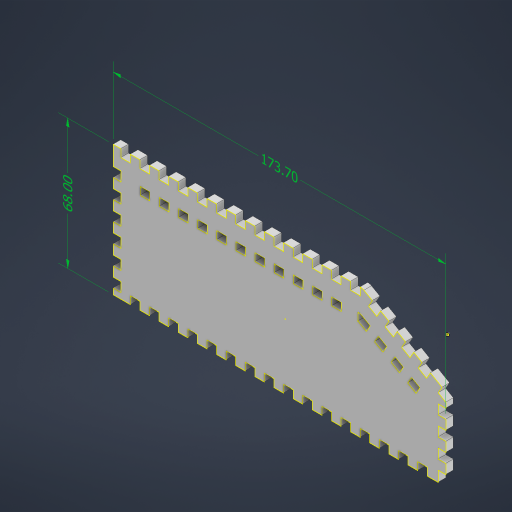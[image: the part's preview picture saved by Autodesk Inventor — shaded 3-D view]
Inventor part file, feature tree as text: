
AUTODESK INVENTOR PART (.ipt)
format: ipt  version: 2023 (Build 270158030, 158C)  size: 1,006,080 bytes
history: native  units: mm
features: extrude x5, sketch x5, other x3, direct_edit x3, move_body x3, delete_face x1, projected_geometry x1
ambient origin geometry x8: Origin, YZ Plane, XZ Plane, XY Plane, X Axis, Y Axis, Z Axis, Center Point
bodies: Solid1 (feature_tree)
feature tree (21):
  other  "Annotations"
  extrude  "Extrusion1"  Depth=60.0mm
  sketch  "Sketch2"  dims[d2=47.0mm d3=30.0deg]
  extrude  "Extrusion2"  TaperAngle=30.0deg  [1 undecoded]
  extrude  "Extrusion3"  Depth=4.0mm TaperAngle=0.0deg
  extrude  "Extrusion4"  Depth=4.0mm
  extrude  "Extrusion5"  Depth=5.0mm
  direct_edit  "Direct Edit1"
  delete_face  "Delete Face1"
  direct_edit  "Direct Edit2"
  direct_edit  "Direct Edit3"
  sketch  "Sketch7"  dims[d9=120.0mm d11=10.0mm d12=10.0mm d14=10.0mm d16=5.0mm d17=4.0mm d18=50.0mm d20=10.0mm d21=10.0mm d23=10.0mm d25=7.0mm d26=5.0mm d27=4.0mm d28=120.0mm d30=10.0mm d31=10.0mm d33=10.0mm d35=5.0mm d36=30.0deg d37=4.0mm d38=40.0mm d40=10.0mm d41=10.0mm d43=10.0mm d45=5.0mm d46=4.0mm d47=170.0mm d49=10.0mm d50=10.0mm d52=10.0mm d54=4.0mm d55=0.0mm d56=4.0mm d57=0.0mm d58=4.0mm d59=10.0mm d60=4.0mm d61=5.0mm d62=60.0mm d64=10.0mm d65=10.0mm d67=10.0mm d69=4.0mm d70=0.0mm d71=5.0mm d72=5.0mm d73=4.0mm d74=4.0mm d75=5.0mm d76=30.0mm d78=10.0mm d79=10.0mm d81=10.0mm d83=4.0mm d84=0.0mm d91=-9.75mm d92=0.0mm d93=16.75mm d94=-1.25mm d95=0.0mm d96=0.0mm d97=-3.75mm d98=0.0mm d99=0.0mm d85=2.396448mm d86=5.019131mm d87=68.0mm d88=5.652543mm d89=4.315711mm d90=173.703194mm]
  sketch  "Sketch1"  dims[d0=172.0mm d1=60.0mm]
  sketch  "Sketch3"  dims[d4=125.0mm d5=4.0mm d6=0.0mm]
  sketch  "Sketch4"  dims[d7=5.0mm d8=4.0mm]
  projected_geometry  "Projected Loop3"
  move_body  "Move1"
  move_body  "Move2"
  move_body  "Move3"
  other  "Linear Dimension 1"
  other  "Linear Dimension 2"
note: 1 required parameter value undecoded (feature->parameter linkage not recoverable at this tier; creation-order binding heuristic only, values carry confidence <= 0.55)
